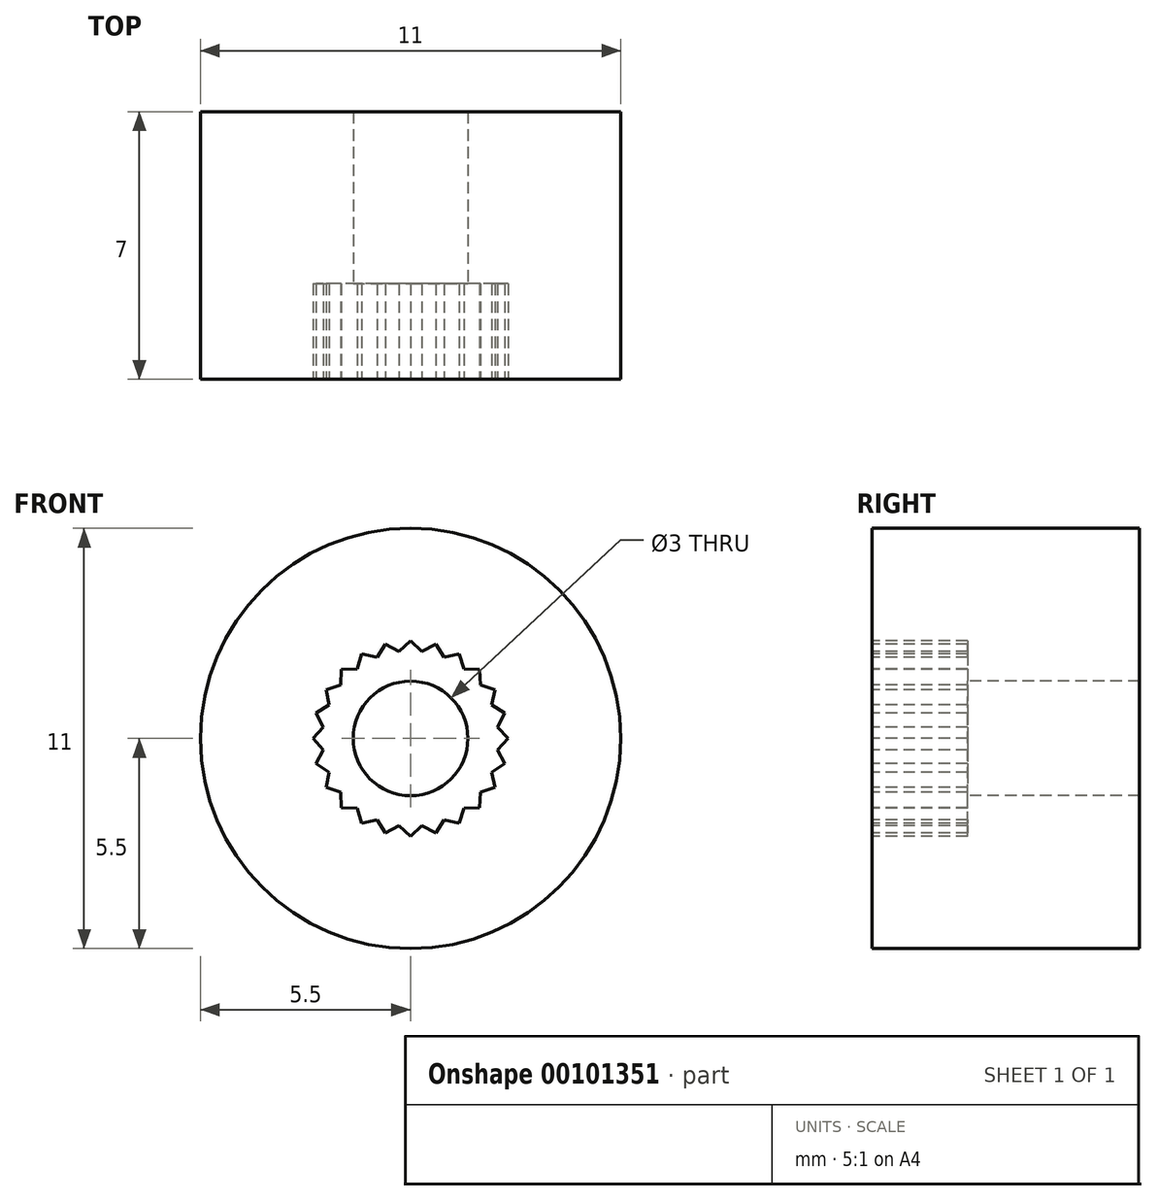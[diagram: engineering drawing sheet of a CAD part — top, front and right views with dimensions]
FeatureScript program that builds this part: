
annotation { "Feature Type Name" : "Feature", "Feature Type Description" : "" }
export const myFeature = defineFeature(function(context is Context, id is Id, definition is map)
    precondition{}
    {
        {
            var Q0;
            Q0=qCreatedBy(makeId("Front.planeOp"),FACE);
            var sketch = newSketch(context, id + "F0", { "sketchPlane" : qUnion([Q0])});
            skCircle(sketch, "E0", {"center": v(0, 0) * mm, "radius": 5.5 * mm});
            skSolve(sketch);
        }
        {
            var Q0;
            Q0 = qSketchRegion(id + "F0", true);
            extrude(context, id + "F1", {"entities" : qUnion([Q0]), "depth" : 7 * mm});
        }
        {
            var Q0;
            Q0=makeQuery(id+"F1.opExtrude","CAP_FACE",FACE,{"disambiguationData":[OSD([sQuery(id+"F0.wireOp",EDGE,"E0")])],"isStart":false});
            var sketch = newSketch(context, id + "F2", { "sketchPlane" : qUnion([Q0])});
            skCircle(sketch, "E1", {"center": v(0, 0) * mm, "radius": 2.3 * mm, "construction": true});
            skFitSpline(sketch, "E2.4", {"points": [v(-0.66, 2.47) * mm, v(-0.54, 2.4) * mm, v(-0.42, 2.34) * mm, v(-0.3, 2.28) * mm]});
            skFitSpline(sketch, "E2.18", {"points": [v(2.28, -0.3) * mm, v(2.34, -0.42) * mm, v(2.4, -0.54) * mm, v(2.47, -0.66) * mm]});
            skFitSpline(sketch, "E2.32", {"points": [v(-0.66, -2.47) * mm, v(-0.73, -2.35) * mm, v(-0.8, -2.24) * mm, v(-0.88, -2.12) * mm]});
            skFitSpline(sketch, "E2.33", {"points": [v(-0.88, -2.12) * mm, v(-1.01, -2.15) * mm, v(-1.15, -2.18) * mm, v(-1.28, -2.21) * mm]});
            skFitSpline(sketch, "E2.7", {"points": [v(0.3, 2.28) * mm, v(0.42, 2.34) * mm, v(0.54, 2.4) * mm, v(0.66, 2.47) * mm]});
            skCircle(sketch, "E3", {"center": v(0, 0) * mm, "radius": 2.56 * mm, "construction": true});
            skFitSpline(sketch, "E2.34", {"points": [v(-1.28, -2.21) * mm, v(-1.32, -2.08) * mm, v(-1.36, -1.95) * mm, v(-1.4, -1.82) * mm]});
            skFitSpline(sketch, "E2.16", {"points": [v(2.47, 0.66) * mm, v(2.4, 0.54) * mm, v(2.34, 0.42) * mm, v(2.28, 0.3) * mm]});
            skFitSpline(sketch, "E2.13", {"points": [v(1.82, 1.4) * mm, v(1.95, 1.36) * mm, v(2.08, 1.32) * mm, v(2.21, 1.28) * mm]});
            skFitSpline(sketch, "E2.25", {"points": [v(1.4, -1.82) * mm, v(1.36, -1.95) * mm, v(1.32, -2.08) * mm, v(1.28, -2.21) * mm]});
            skFitSpline(sketch, "E2.38", {"points": [v(-2.21, -1.28) * mm, v(-2.18, -1.15) * mm, v(-2.15, -1.01) * mm, v(-2.12, -0.88) * mm]});
            skFitSpline(sketch, "E2.14", {"points": [v(2.21, 1.28) * mm, v(2.18, 1.15) * mm, v(2.15, 1.01) * mm, v(2.12, 0.88) * mm]});
            skFitSpline(sketch, "E2.12", {"points": [v(1.8, 1.8) * mm, v(1.81, 1.67) * mm, v(1.82, 1.54) * mm, v(1.82, 1.4) * mm]});
            skFitSpline(sketch, "E2.31", {"points": [v(-0.3, -2.28) * mm, v(-0.42, -2.34) * mm, v(-0.54, -2.4) * mm, v(-0.66, -2.47) * mm]});
            skFitSpline(sketch, "E2.8", {"points": [v(0.66, 2.47) * mm, v(0.73, 2.35) * mm, v(0.8, 2.24) * mm, v(0.88, 2.12) * mm]});
            skFitSpline(sketch, "E2.39", {"points": [v(-2.12, -0.88) * mm, v(-2.24, -0.8) * mm, v(-2.35, -0.73) * mm, v(-2.47, -0.66) * mm]});
            skFitSpline(sketch, "E2.23", {"points": [v(1.82, -1.4) * mm, v(1.82, -1.54) * mm, v(1.81, -1.67) * mm, v(1.8, -1.8) * mm]});
            skFitSpline(sketch, "E2.47", {"points": [v(-2.12, 0.88) * mm, v(-2.15, 1.01) * mm, v(-2.18, 1.15) * mm, v(-2.21, 1.28) * mm]});
            skFitSpline(sketch, "E2.9", {"points": [v(0.88, 2.12) * mm, v(1.01, 2.15) * mm, v(1.15, 2.18) * mm, v(1.28, 2.21) * mm]});
            skFitSpline(sketch, "E2.36", {"points": [v(-1.8, -1.8) * mm, v(-1.81, -1.67) * mm, v(-1.82, -1.54) * mm, v(-1.82, -1.4) * mm]});
            skFitSpline(sketch, "E2.20", {"points": [v(2.47, -0.66) * mm, v(2.35, -0.73) * mm, v(2.24, -0.8) * mm, v(2.12, -0.88) * mm]});
            skFitSpline(sketch, "E2.15", {"points": [v(2.12, 0.88) * mm, v(2.24, 0.8) * mm, v(2.35, 0.73) * mm, v(2.47, 0.66) * mm]});
            skFitSpline(sketch, "E2.2", {"points": [v(-1.28, 2.21) * mm, v(-1.15, 2.18) * mm, v(-1.01, 2.15) * mm, v(-0.88, 2.12) * mm]});
            skFitSpline(sketch, "E2.26", {"points": [v(1.28, -2.21) * mm, v(1.15, -2.18) * mm, v(1.01, -2.15) * mm, v(0.88, -2.12) * mm]});
            skFitSpline(sketch, "E2.30", {"points": [v(0, -2.56) * mm, v(-0.1, -2.46) * mm, v(-0.2, -2.37) * mm, v(-0.3, -2.28) * mm]});
            skFitSpline(sketch, "E2.43", {"points": [v(-2.28, 0.3) * mm, v(-2.34, 0.42) * mm, v(-2.4, 0.54) * mm, v(-2.47, 0.66) * mm]});
            skFitSpline(sketch, "E2.10", {"points": [v(1.28, 2.21) * mm, v(1.32, 2.08) * mm, v(1.36, 1.95) * mm, v(1.4, 1.82) * mm]});
            skFitSpline(sketch, "E2.11", {"points": [v(1.4, 1.82) * mm, v(1.54, 1.82) * mm, v(1.67, 1.81) * mm, v(1.8, 1.8) * mm]});
            skFitSpline(sketch, "E2.35", {"points": [v(-1.4, -1.82) * mm, v(-1.54, -1.82) * mm, v(-1.67, -1.81) * mm, v(-1.8, -1.8) * mm]});
            skFitSpline(sketch, "E2.21", {"points": [v(2.12, -0.88) * mm, v(2.15, -1.01) * mm, v(2.18, -1.15) * mm, v(2.21, -1.28) * mm]});
            skFitSpline(sketch, "E2.37", {"points": [v(-1.82, -1.4) * mm, v(-1.95, -1.36) * mm, v(-2.08, -1.32) * mm, v(-2.21, -1.28) * mm]});
            skFitSpline(sketch, "E2.40", {"points": [v(-2.47, -0.66) * mm, v(-2.4, -0.54) * mm, v(-2.34, -0.42) * mm, v(-2.28, -0.3) * mm]});
            skFitSpline(sketch, "E2.24", {"points": [v(1.8, -1.8) * mm, v(1.67, -1.81) * mm, v(1.54, -1.82) * mm, v(1.4, -1.82) * mm]});
            skFitSpline(sketch, "E2.29", {"points": [v(0.3, -2.28) * mm, v(0.2, -2.37) * mm, v(0.1, -2.46) * mm, v(0, -2.56) * mm]});
            skFitSpline(sketch, "E2.45", {"points": [v(-1.82, 1.4) * mm, v(-1.82, 1.54) * mm, v(-1.81, 1.67) * mm, v(-1.8, 1.8) * mm]});
            skFitSpline(sketch, "E2.41", {"points": [v(-2.28, -0.3) * mm, v(-2.37, -0.2) * mm, v(-2.46, -0.1) * mm, v(-2.56, 0) * mm]});
            skFitSpline(sketch, "E2.44", {"points": [v(-2.47, 0.66) * mm, v(-2.35, 0.73) * mm, v(-2.24, 0.8) * mm, v(-2.12, 0.88) * mm]});
            skFitSpline(sketch, "E2.28", {"points": [v(0.66, -2.47) * mm, v(0.54, -2.4) * mm, v(0.42, -2.34) * mm, v(0.3, -2.28) * mm]});
            skFitSpline(sketch, "E2.0", {"points": [v(-1.8, 1.8) * mm, v(-1.67, 1.81) * mm, v(-1.54, 1.82) * mm, v(-1.4, 1.82) * mm]});
            skFitSpline(sketch, "E2.5", {"points": [v(-0.3, 2.28) * mm, v(-0.2, 2.37) * mm, v(-0.1, 2.46) * mm, v(0, 2.56) * mm]});
            skFitSpline(sketch, "E2.27", {"points": [v(0.88, -2.12) * mm, v(0.8, -2.24) * mm, v(0.73, -2.35) * mm, v(0.66, -2.47) * mm]});
            skFitSpline(sketch, "E2.1", {"points": [v(-1.4, 1.82) * mm, v(-1.36, 1.95) * mm, v(-1.32, 2.08) * mm, v(-1.28, 2.21) * mm]});
            skFitSpline(sketch, "E2.6", {"points": [v(0, 2.56) * mm, v(0.1, 2.46) * mm, v(0.2, 2.37) * mm, v(0.3, 2.28) * mm]});
            skFitSpline(sketch, "E2.22", {"points": [v(2.21, -1.28) * mm, v(2.08, -1.32) * mm, v(1.95, -1.36) * mm, v(1.82, -1.4) * mm]});
            skFitSpline(sketch, "E2.42", {"points": [v(-2.56, 0) * mm, v(-2.46, 0.1) * mm, v(-2.37, 0.2) * mm, v(-2.28, 0.3) * mm]});
            skFitSpline(sketch, "E2.3", {"points": [v(-0.88, 2.12) * mm, v(-0.8, 2.24) * mm, v(-0.73, 2.35) * mm, v(-0.66, 2.47) * mm]});
            skFitSpline(sketch, "E2.17", {"points": [v(2.28, 0.3) * mm, v(2.37, 0.2) * mm, v(2.46, 0.1) * mm, v(2.56, 0) * mm]});
            skFitSpline(sketch, "E2.46", {"points": [v(-2.21, 1.28) * mm, v(-2.08, 1.32) * mm, v(-1.95, 1.36) * mm, v(-1.82, 1.4) * mm]});
            skFitSpline(sketch, "E2.19", {"points": [v(2.56, 0) * mm, v(2.46, -0.1) * mm, v(2.37, -0.2) * mm, v(2.28, -0.3) * mm]});
            skLineSegment(sketch, "E4", {"start": v(-1.82, 1.4) * mm, "end": v(1.82, -1.4) * mm, "construction": true});
            skCircle(sketch, "E5", {"center": v(0, 0) * mm, "radius": 1.5 * mm});
            skSolve(sketch);
        }
        {
            var Q0;
            Q0=makeQuery(id+"F2.imprint","IMPRINT",FACE,{"disambiguationData":[TD([[makeQuery(id+"F2.imprint","IMPRINT",EDGE,{"derivedFrom":sQuery(id+"F2.wireOp",EDGE,"E2.4")}),-1.0]])]});
            extrude(context, id + "F3", {"entities" : qUnion([Q0]), "operationType" : NewBodyOperationType.REMOVE, "oppositeDirection" : true, "depth" : 2.5 * mm});
        }
        {
            var Q0;
            Q0=makeQuery(id+"F3.boolean.opBoolean","SPLIT",FACE,{"disambiguationData":[TD([makeQuery(id+"F3.opExtrude","SWEPT_FACE",FACE,{"disambiguationData":[OSD([sQuery(id+"F2.wireOp",EDGE,"E5")])]})])],"derivedFrom":makeQuery(id+"F1.opExtrude","CAP_FACE",FACE,{"disambiguationData":[OSD([sQuery(id+"F0.wireOp",EDGE,"E0")])],"isStart":false})});
            extrude(context, id + "F4", {"entities" : qUnion([Q0]), "operationType" : NewBodyOperationType.REMOVE, "endBound" : BoundingType.THROUGH_ALL, "oppositeDirection" : true, "depth" : 25 * mm});
        }
    });
